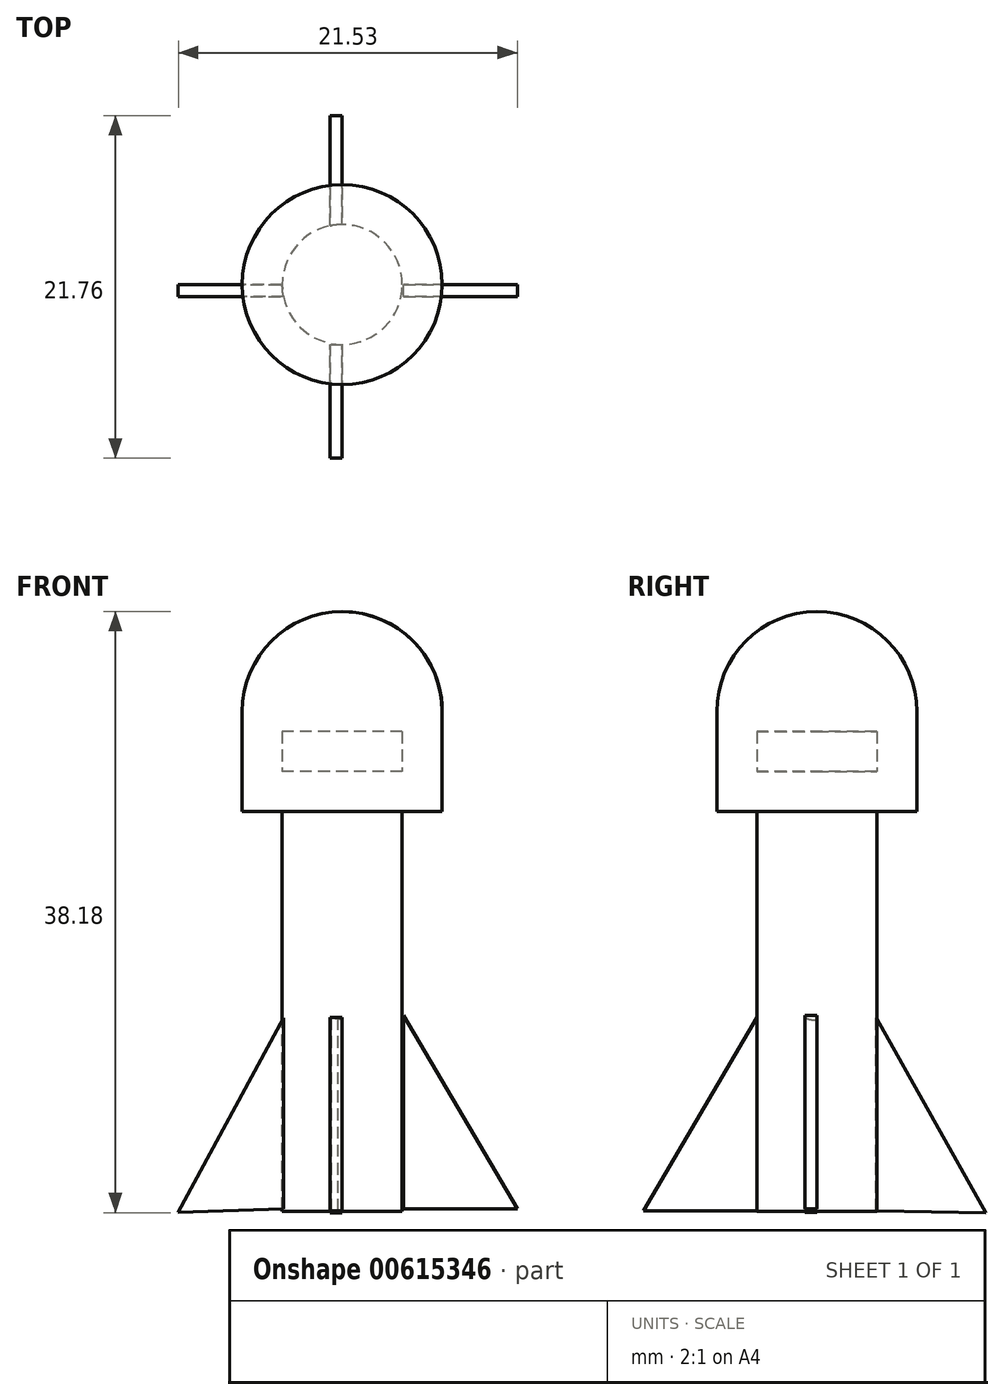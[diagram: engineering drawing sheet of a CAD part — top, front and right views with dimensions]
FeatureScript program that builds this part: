
annotation { "Feature Type Name" : "Feature", "Feature Type Description" : "" }
export const myFeature = defineFeature(function(context is Context, id is Id, definition is map)
    precondition{}
    {
        {
            var Q0;
            Q0=qCreatedBy(makeId("Top.planeOp"),FACE);
            var sketch = newSketch(context, id + "F0", { "sketchPlane" : qUnion([Q0])});
            skCircle(sketch, "E0", {"center": v(0, 0) * mm, "radius": 6.35 * mm});
            skSolve(sketch);
        }
        {
            var Q0;
            Q0 = qSketchRegion(id + "F0", true);
            extrude(context, id + "F1", {"entities" : qUnion([Q0]), "depth" : 5.08 * mm, "offsetDistance" : 25.4 * mm});
        }
        {
            var Q0;
            Q0=makeQuery(id+"F1.opExtrude","CAP_FACE",FACE,{"disambiguationData":[OSD([sQuery(id+"F0.wireOp",EDGE,"E0")])],"isStart":false});
            shell(context, id + "F2", {"entities" : qUnion([Q0]), "thickness" : 2.54 * mm});
        }
        {
            var Q0;
            Q0=makeQuery(id+"F1.opExtrude","CAP_FACE",FACE,{"disambiguationData":[OSD([sQuery(id+"F0.wireOp",EDGE,"E0")])],"isStart":false});
            var sketch = newSketch(context, id + "F3", { "sketchPlane" : qUnion([Q0])});
            skCircle(sketch, "E1", {"center": v(0, 0) * mm, "radius": 6.35 * mm});
            skSolve(sketch);
        }
        {
            var Q0;
            Q0 = qSketchRegion(id + "F3", true);
            extrude(context, id + "F4", {"entities" : qUnion([Q0]), "operationType" : NewBodyOperationType.ADD, "depth" : 7.62 * mm, "offsetDistance" : 25.4 * mm});
        }
        {
            var Q0;
            Q0=makeQuery(id+"F4.opExtrude","CAP_EDGE",EDGE,{"disambiguationData":[OSD([sQuery(id+"F3.wireOp",EDGE,"E1")])],"isStart":false});
            fillet(context, id + "F5", {"entities" : qUnion([Q0]), "radius" : 6.35 * mm, "tangentPropagation" : true, "allowEdgeOverflow" : false});
        }
        {
            var Q0;
            Q0=makeQuery(id+"F1.opExtrude","CAP_FACE",FACE,{"disambiguationData":[OSD([sQuery(id+"F0.wireOp",EDGE,"E0")])],"isStart":true});
            var sketch = newSketch(context, id + "F6", { "sketchPlane" : qUnion([Q0])});
            skCircle(sketch, "E2", {"center": v(0, 0) * mm, "radius": 3.81 * mm});
            skSolve(sketch);
        }
        {
            var Q0;
            Q0=makeQuery(id+"F6.imprint","IMPRINT",FACE,{"disambiguationData":[TD([[makeQuery(id+"F6.imprint","IMPRINT",EDGE,{"derivedFrom":sQuery(id+"F6.wireOp",EDGE,"E2")}),1.0]])]});
            extrude(context, id + "F7", {"entities" : qUnion([Q0]), "operationType" : NewBodyOperationType.ADD, "depth" : 25.4 * mm, "offsetDistance" : 25.4 * mm});
        }
        {
            var Q0;
            Q0=qCreatedBy(makeId("Right.planeOp"),FACE);
            var sketch = newSketch(context, id + "F8", { "sketchPlane" : qUnion([Q0])});
            skLineSegment(sketch, "E3", {"start": v(3.75, -25.37) * mm, "end": v(3.75, -13.08) * mm});
            skLineSegment(sketch, "E4", {"start": v(3.75, -13.08) * mm, "end": v(10.74, -25.48) * mm});
            skLineSegment(sketch, "E5", {"start": v(10.74, -25.48) * mm, "end": v(3.75, -25.37) * mm});
            skLineSegment(sketch, "E6", {"start": v(-3.8, -25.37) * mm, "end": v(-3.8, -13.08) * mm});
            skLineSegment(sketch, "E7", {"start": v(-3.8, -13.08) * mm, "end": v(-11.02, -25.37) * mm});
            skLineSegment(sketch, "E8", {"start": v(-11.02, -25.37) * mm, "end": v(-3.8, -25.37) * mm});
            skSolve(sketch);
        }
        {
            var Q0;
            Q0 = qSketchRegion(id + "F8", true);
            extrude(context, id + "F9", {"entities" : qUnion([Q0]), "operationType" : NewBodyOperationType.ADD, "oppositeDirection" : true, "depth" : 0.76 * mm, "offsetDistance" : 25.4 * mm});
        }
        {
            var Q0;
            Q0=qCreatedBy(makeId("Front.planeOp"),FACE);
            var sketch = newSketch(context, id + "F10", { "sketchPlane" : qUnion([Q0])});
            skLineSegment(sketch, "E9", {"start": v(-3.65, -25.24) * mm, "end": v(-3.65, -12.96) * mm});
            skLineSegment(sketch, "E10", {"start": v(-3.65, -12.96) * mm, "end": v(-10.41, -25.47) * mm});
            skLineSegment(sketch, "E11", {"start": v(-10.41, -25.47) * mm, "end": v(-3.65, -25.24) * mm});
            skLineSegment(sketch, "E12", {"start": v(3.9, -25.24) * mm, "end": v(3.9, -12.96) * mm});
            skLineSegment(sketch, "E13", {"start": v(3.9, -12.96) * mm, "end": v(11.12, -25.24) * mm});
            skLineSegment(sketch, "E14", {"start": v(11.12, -25.24) * mm, "end": v(3.9, -25.24) * mm});
            skSolve(sketch);
        }
        {
            var Q0;
            Q0 = qSketchRegion(id + "F10", true);
            extrude(context, id + "F11", {"entities" : qUnion([Q0]), "operationType" : NewBodyOperationType.ADD, "depth" : 0.76 * mm, "offsetDistance" : 25.4 * mm});
        }
    });
